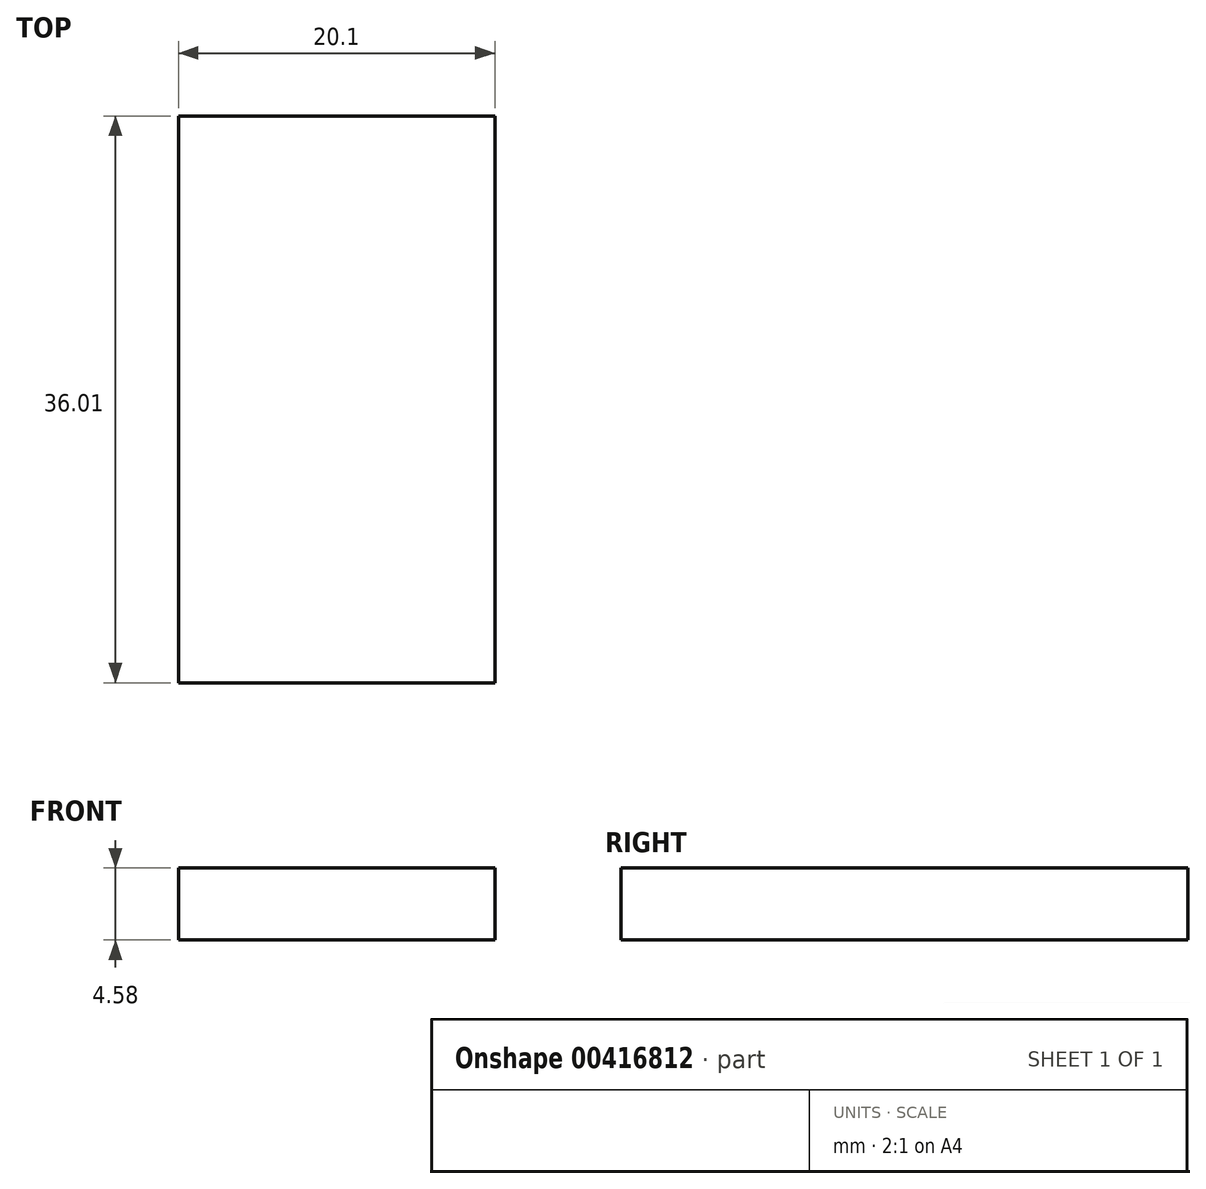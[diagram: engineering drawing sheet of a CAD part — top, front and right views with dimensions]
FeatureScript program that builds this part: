
annotation { "Feature Type Name" : "Feature", "Feature Type Description" : "" }
export const myFeature = defineFeature(function(context is Context, id is Id, definition is map)
    precondition{}
    {
        {
            var Q0;
            Q0=qCreatedBy(makeId("Top.planeOp"),FACE);
            var sketch = newSketch(context, id + "F0", { "sketchPlane" : qUnion([Q0])});
            skLineSegment(sketch, "E0.bottom", {"start": v(0, 0) * mm, "end": v(20.1, 0) * mm});
            skLineSegment(sketch, "E0.top", {"start": v(0, 36) * mm, "end": v(20.1, 36) * mm});
            skLineSegment(sketch, "E0.left", {"start": v(0, 0) * mm, "end": v(0, 36) * mm});
            skLineSegment(sketch, "E0.right", {"start": v(20.1, 0) * mm, "end": v(20.1, 36) * mm});
            skSolve(sketch);
        }
        {
            var Q0;
            Q0 = qSketchRegion(id + "F0", true);
            extrude(context, id + "F1", {"entities" : qUnion([Q0]), "depth" : 4.58 * mm, "offsetDistance" : 25.4 * mm});
        }
    });
